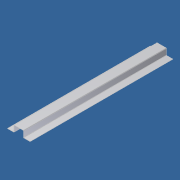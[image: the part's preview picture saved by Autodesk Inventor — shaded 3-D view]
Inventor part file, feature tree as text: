
AUTODESK INVENTOR PART (.ipt)
format: ipt  version: 2012 (Build 160160000, 160)  size: 98,304 bytes
history: native  units: in
note: dims shown in document units (in); Inventor stores cm internally (conversion verified against a paired STEP export)
features: extrude x1, sketch x1
ambient origin geometry x8: Origin, YZ Plane, XZ Plane, XY Plane, X Axis, Y Axis, Z Axis, Center Point
bodies: Solid1 (feature_tree)
feature tree (2):
  extrude  "Extrusion1"  Depth=0.1196in
  sketch  "Sketch1"  dims[d0=0.25in d1=0.1196in d2=6.0in d4=88.0in d5=0.0in d6=0.12in d7=4.0in d8=0.125in d9=4.0in d10=0.12in d11=0.125in d12=4.0in d13=4.0in]
